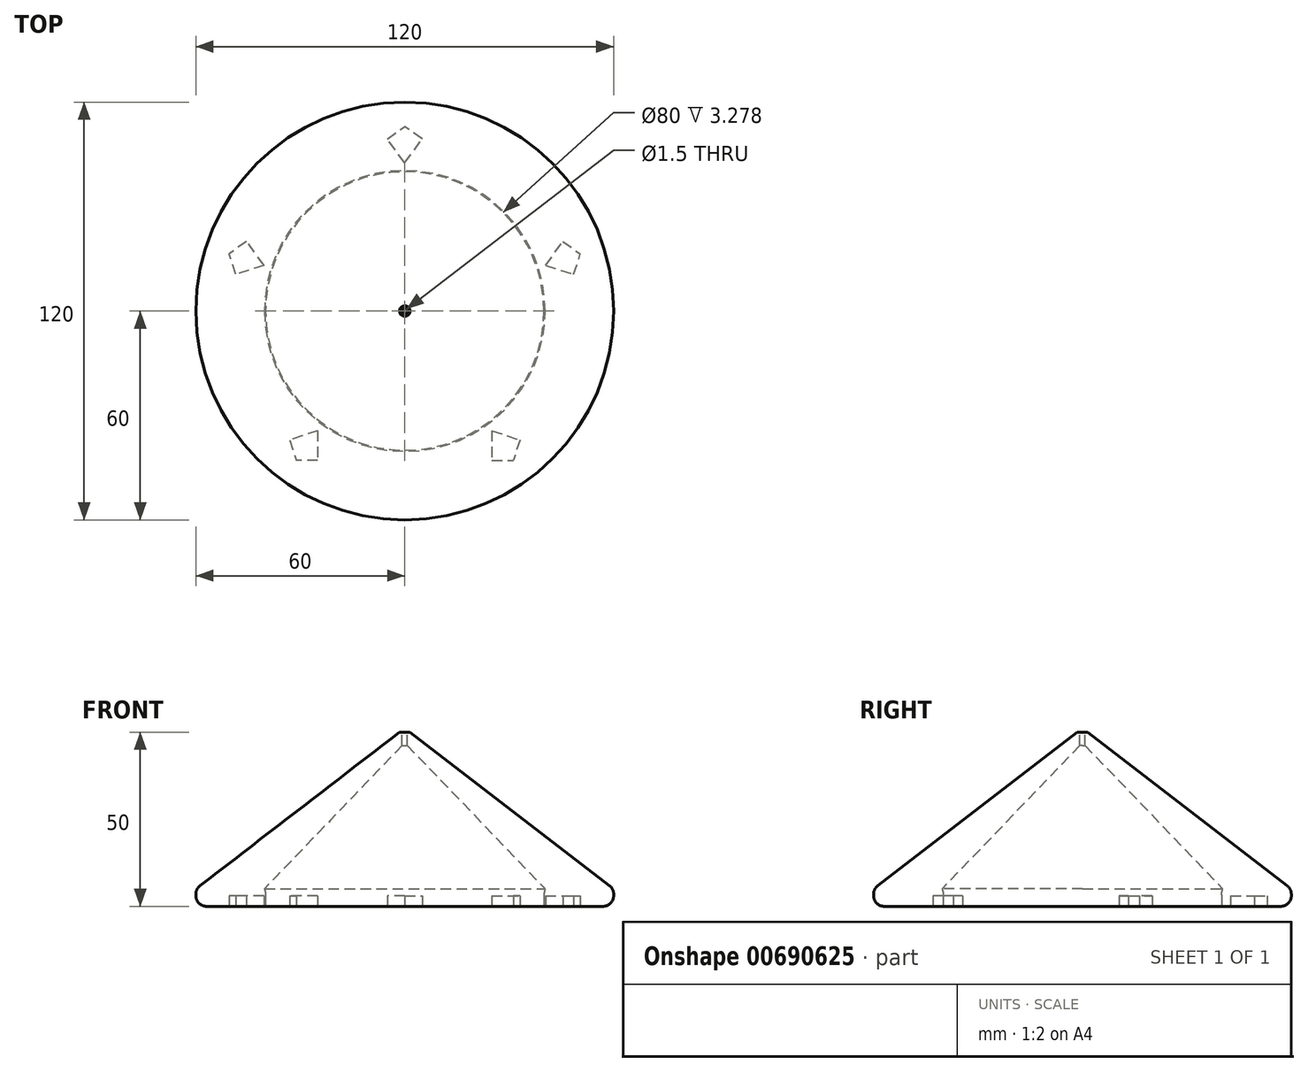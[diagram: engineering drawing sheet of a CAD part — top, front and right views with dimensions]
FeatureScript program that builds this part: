
annotation { "Feature Type Name" : "Feature", "Feature Type Description" : "" }
export const myFeature = defineFeature(function(context is Context, id is Id, definition is map)
    precondition{}
    {
        {
            var Q0;
            Q0=qCreatedBy(makeId("Top.planeOp"),FACE);
            var sketch = newSketch(context, id + "F0", { "sketchPlane" : qUnion([Q0])});
            skCircle(sketch, "E0.cCircle", {"center": v(0, 0) * mm, "radius": 34.4 * mm, "construction": true});
            skLineSegment(sketch, "E0.0", {"start": v(25, -34.4) * mm, "end": v(-25, -34.4) * mm, "construction": true});
            skLineSegment(sketch, "E0.1", {"start": v(-25, -34.4) * mm, "end": v(-40.45, 13.14) * mm, "construction": true});
            skLineSegment(sketch, "E0.2", {"start": v(-40.45, 13.14) * mm, "end": v(0, 42.53) * mm, "construction": true});
            skLineSegment(sketch, "E0.3", {"start": v(0, 42.53) * mm, "end": v(40.45, 13.14) * mm, "construction": true});
            skLineSegment(sketch, "E0.4", {"start": v(40.45, 13.14) * mm, "end": v(25, -34.4) * mm, "construction": true});
            skPoint(sketch, "E0.0.midPoint", {"position": v(0, -34.4) * mm});
            skLineSegment(sketch, "E1.0", {"start": v(48.53, 10.52) * mm, "end": v(33.08, -37.04) * mm});
            skLineSegment(sketch, "E2.0", {"start": v(25, -42.9) * mm, "end": v(-25, -42.9) * mm});
            skLineSegment(sketch, "E3", {"start": v(25, -34.4) * mm, "end": v(25, -42.9) * mm});
            skLineSegment(sketch, "E4", {"start": v(25, -34.4) * mm, "end": v(33.08, -37.04) * mm});
            skLineSegment(sketch, "E5", {"start": v(25, -42.9) * mm, "end": v(31.18, -42.9) * mm});
            skLineSegment(sketch, "E6", {"start": v(33.08, -37.04) * mm, "end": v(31.18, -42.9) * mm});
            skLineSegment(sketch, "E7.1.0", {"start": v(40.45, 13.14) * mm, "end": v(48.53, 10.52) * mm});
            skLineSegment(sketch, "E7.1.1", {"start": v(48.53, 10.52) * mm, "end": v(50.44, 16.39) * mm});
            skLineSegment(sketch, "E7.1.2", {"start": v(45.45, 20.02) * mm, "end": v(50.44, 16.39) * mm});
            skLineSegment(sketch, "E7.1.3", {"start": v(40.45, 13.14) * mm, "end": v(45.45, 20.02) * mm});
            skLineSegment(sketch, "E7.2.0", {"start": v(0, 42.53) * mm, "end": v(5, 49.4) * mm});
            skLineSegment(sketch, "E7.2.1", {"start": v(5, 49.4) * mm, "end": v(0, 53.04) * mm});
            skLineSegment(sketch, "E7.2.2", {"start": v(-5, 49.4) * mm, "end": v(0, 53.04) * mm});
            skLineSegment(sketch, "E7.2.3", {"start": v(0, 42.53) * mm, "end": v(-5, 49.4) * mm});
            skLineSegment(sketch, "E7.3.0", {"start": v(-40.45, 13.14) * mm, "end": v(-45.45, 20.02) * mm});
            skLineSegment(sketch, "E7.3.1", {"start": v(-45.45, 20.02) * mm, "end": v(-50.44, 16.39) * mm});
            skLineSegment(sketch, "E7.3.2", {"start": v(-48.53, 10.52) * mm, "end": v(-50.44, 16.39) * mm});
            skLineSegment(sketch, "E7.3.3", {"start": v(-40.45, 13.14) * mm, "end": v(-48.53, 10.52) * mm});
            skLineSegment(sketch, "E7.4.0", {"start": v(-25, -34.4) * mm, "end": v(-33.08, -37.04) * mm});
            skLineSegment(sketch, "E7.4.1", {"start": v(-33.08, -37.04) * mm, "end": v(-31.18, -42.9) * mm});
            skLineSegment(sketch, "E7.4.2", {"start": v(-25, -42.9) * mm, "end": v(-31.18, -42.9) * mm});
            skLineSegment(sketch, "E7.4.3", {"start": v(-25, -34.4) * mm, "end": v(-25, -42.9) * mm});
            skCircle(sketch, "E8", {"center": v(0, 0) * mm, "radius": 60 * mm});
            skCircle(sketch, "E9", {"center": v(0, 0) * mm, "radius": 40 * mm});
            skSolve(sketch);
        }
        {
            var Q0;
            Q0=qCreatedBy(makeId("Top.planeOp"),FACE);
            cPlane(context, id + "F1", {"entities" : qUnion([Q0]), "cplaneType" : CPlaneType.OFFSET, "offset" : 50 * mm, "width" : 150 * mm, "height" : 150 * mm});
        }
        {
            var Q0;
            Q0=qCreatedBy(id+"F1.planeOp",FACE);
            var sketch = newSketch(context, id + "F2", { "sketchPlane" : qUnion([Q0])});
            skCircle(sketch, "E10", {"center": v(0, 0) * mm, "radius": 1 * mm});
            skSolve(sketch);
        }
        {
            var Q0;
            Q0=makeQuery(id+"F0.imprint","IMPRINT",FACE,{"disambiguationData":[TD([[makeQuery(id+"F0.imprint","IMPRINT",EDGE,{"derivedFrom":sQuery(id+"F0.wireOp",EDGE,"E1.0")}),1.0]])]});
            var Q1;
            Q1=makeQuery(id+"F0.imprint","IMPRINT",FACE,{"disambiguationData":[TD([[makeQuery(id+"F0.imprint","IMPRINT",EDGE,{"derivedFrom":sQuery(id+"F0.wireOp",EDGE,"E3")}),-1.0]])]});
            extrude(context, id + "F3", {"entities" : qUnion([Q0, Q1]), "depth" : 3 * mm, "offsetDistance" : 25 * mm});
        }
        {
            var Q0;
            Q0=makeQuery(id+"F3.opExtrude","CAP_FACE",FACE,{"disambiguationData":[OSD([sQuery(id+"F0.wireOp",EDGE,"E3"),sQuery(id+"F0.wireOp",EDGE,"E4"),sQuery(id+"F0.wireOp",EDGE,"E5"),sQuery(id+"F0.wireOp",EDGE,"E6"),sQuery(id+"F0.wireOp",EDGE,"E7.1.0"),sQuery(id+"F0.wireOp",EDGE,"E7.1.1"),sQuery(id+"F0.wireOp",EDGE,"E7.1.2"),sQuery(id+"F0.wireOp",EDGE,"E7.1.3"),sQuery(id+"F0.wireOp",EDGE,"E7.2.0"),sQuery(id+"F0.wireOp",EDGE,"E7.2.1"),sQuery(id+"F0.wireOp",EDGE,"E7.2.2"),sQuery(id+"F0.wireOp",EDGE,"E7.2.3"),sQuery(id+"F0.wireOp",EDGE,"E7.3.0"),sQuery(id+"F0.wireOp",EDGE,"E7.3.1"),sQuery(id+"F0.wireOp",EDGE,"E7.3.2"),sQuery(id+"F0.wireOp",EDGE,"E7.3.3"),sQuery(id+"F0.wireOp",EDGE,"E7.4.0"),sQuery(id+"F0.wireOp",EDGE,"E7.4.1"),sQuery(id+"F0.wireOp",EDGE,"E7.4.2"),sQuery(id+"F0.wireOp",EDGE,"E7.4.3"),sQuery(id+"F0.wireOp",EDGE,"E8"),sQuery(id+"F0.wireOp",EDGE,"E9")])],"isStart":false});
            var sketch = newSketch(context, id + "F4", { "sketchPlane" : qUnion([Q0])});
            skCircle(sketch, "E11", {"center": v(0, 0) * mm, "radius": 60 * mm});
            skCircle(sketch, "E12", {"center": v(0, 0) * mm, "radius": 40 * mm});
            skSolve(sketch);
        }
        {
            var Q0;
            Q0=makeQuery(id+"F4.imprint","IMPRINT",FACE,{"disambiguationData":[TD([[makeQuery(id+"F4.imprint","IMPRINT",EDGE,{"derivedFrom":sQuery(id+"F4.wireOp",EDGE,"E11")}),1.0]])]});
            var Q1;
            Q1=makeQuery(id+"F4.imprint","IMPRINT",FACE,{"disambiguationData":[TD([[makeQuery(id+"F4.imprint","IMPRINT",EDGE,{"derivedFrom":makeQuery(id+"F3.opExtrude","CAP_EDGE",EDGE,{"disambiguationData":[OSD([sQuery(id+"F0.wireOp",EDGE,"E7.3.0")])],"isStart":false})}),1.0]])]});
            var Q2;
            Q2=makeQuery(id+"F4.imprint","IMPRINT",FACE,{"disambiguationData":[TD([[makeQuery(id+"F4.imprint","IMPRINT",EDGE,{"derivedFrom":makeQuery(id+"F3.opExtrude","CAP_EDGE",EDGE,{"disambiguationData":[OSD([sQuery(id+"F0.wireOp",EDGE,"E7.2.0")])],"isStart":false})}),1.0]])]});
            var Q3;
            Q3=makeQuery(id+"F4.imprint","IMPRINT",FACE,{"disambiguationData":[TD([[makeQuery(id+"F4.imprint","IMPRINT",EDGE,{"derivedFrom":makeQuery(id+"F3.opExtrude","CAP_EDGE",EDGE,{"disambiguationData":[OSD([sQuery(id+"F0.wireOp",EDGE,"E7.1.0")])],"isStart":false})}),1.0]])]});
            var Q4;
            Q4=makeQuery(id+"F4.imprint","IMPRINT",FACE,{"disambiguationData":[TD([[makeQuery(id+"F4.imprint","IMPRINT",EDGE,{"derivedFrom":makeQuery(id+"F3.opExtrude","CAP_EDGE",EDGE,{"disambiguationData":[OSD([sQuery(id+"F0.wireOp",EDGE,"E3")])],"isStart":false})}),1.0]])]});
            var Q5;
            Q5=makeQuery(id+"F4.imprint","IMPRINT",FACE,{"disambiguationData":[TD([[makeQuery(id+"F4.imprint","IMPRINT",EDGE,{"derivedFrom":makeQuery(id+"F3.opExtrude","CAP_EDGE",EDGE,{"disambiguationData":[OSD([sQuery(id+"F0.wireOp",EDGE,"E7.4.0")])],"isStart":false})}),1.0]])]});
            extrude(context, id + "F5", {"entities" : qUnion([Q0, Q1, Q2, Q3, Q4, Q5]), "operationType" : NewBodyOperationType.ADD, "depth" : 2 * mm, "offsetDistance" : 25 * mm});
        }
        {
            var Q0;
            Q0=qCreatedBy(makeId("Front.planeOp"),FACE);
            var sketch = newSketch(context, id + "F6", { "sketchPlane" : qUnion([Q0])});
            skLineSegment(sketch, "E13", {"start": v(-60, 5) * mm, "end": v(-40.3, 5) * mm});
            skLineSegment(sketch, "E14", {"start": v(-40.3, 5) * mm, "end": v(0, 47) * mm});
            skLineSegment(sketch, "E15", {"start": v(0, 47) * mm, "end": v(0, 50) * mm});
            skLineSegment(sketch, "E16", {"start": v(0, 50) * mm, "end": v(-1.5, 50) * mm});
            skLineSegment(sketch, "E17", {"start": v(-1.5, 50) * mm, "end": v(-60, 5) * mm});
            skSolve(sketch);
        }
        {
            var Q0;
            Q0=qCreatedBy(makeId("Front.planeOp"),FACE);
            var sketch = newSketch(context, id + "F7", { "sketchPlane" : qUnion([Q0])});
            skLineSegment(sketch, "E18", {"start": v(0, 0) * mm, "end": v(0, 38.15) * mm, "construction": true});
            skSolve(sketch);
        }
        {
            var Q0;
            Q0=makeQuery(id+"F6.imprint","IMPRINT",FACE,{"disambiguationData":[TD([[makeQuery(id+"F6.imprint","IMPRINT",EDGE,{"derivedFrom":sQuery(id+"F6.wireOp",EDGE,"E13")}),1.0]])]});
            var Q1;
            Q1=sQuery(id+"F7.wireOp",EDGE,"E18");
            revolve(context, id + "F8", {"operationType" : NewBodyOperationType.ADD, "entities" : qUnion([Q0]), "axis" : qUnion([Q1]), "revolveType" : RevolveType.FULL});
        }
        {
            var Q0;
            Q0=makeQuery(id+"F8.boolean.opBoolean","MERGE",EDGE,{"derivedFrom":[makeQuery(id+"F5.opExtrude","CAP_EDGE",EDGE,{"disambiguationData":[OSD([sQuery(id+"F4.wireOp",EDGE,"E11")])],"isStart":false}),makeQuery(id+"F8.opRevolve","SWEPT_EDGE",EDGE,{"disambiguationData":[OSD([sQuery(id+"F6.wireOp",EDGE,"E13"),sQuery(id+"F6.wireOp",EDGE,"E17")])]})]});
            var Q1;
            Q1=makeQuery(id+"F3.opExtrude","CAP_EDGE",EDGE,{"disambiguationData":[OSD([sQuery(id+"F0.wireOp",EDGE,"E8")])],"isStart":true});
            fillet(context, id + "F9", {"entities" : qUnion([Q0, Q1]), "radius" : 3 * mm, "tangentPropagation" : true, "allowEdgeOverflow" : false});
        }
        {
            var Q0;
            Q0=qCreatedBy(id+"F1.planeOp",FACE);
            var sketch = newSketch(context, id + "F10", { "sketchPlane" : qUnion([Q0])});
            skCircle(sketch, "E19", {"center": v(0, 0) * mm, "radius": 0.75 * mm});
            skSolve(sketch);
        }
        {
            var Q0;
            Q0 = qSketchRegion(id + "F10", true);
            extrude(context, id + "F11", {"entities" : qUnion([Q0]), "operationType" : NewBodyOperationType.REMOVE, "endBound" : BoundingType.THROUGH_ALL, "oppositeDirection" : true, "depth" : 25 * mm, "offsetDistance" : 25 * mm});
        }
        {
            var Q0;
            Q0=makeQuery(id+"F5.opExtrude","CAP_EDGE",EDGE,{"disambiguationData":[OSD([sQuery(id+"F4.wireOp",EDGE,"E12")])],"isStart":false});
            fillet(context, id + "F12", {"entities" : qUnion([Q0]), "radius" : 5 * mm, "tangentPropagation" : true, "allowEdgeOverflow" : false});
        }
    });
